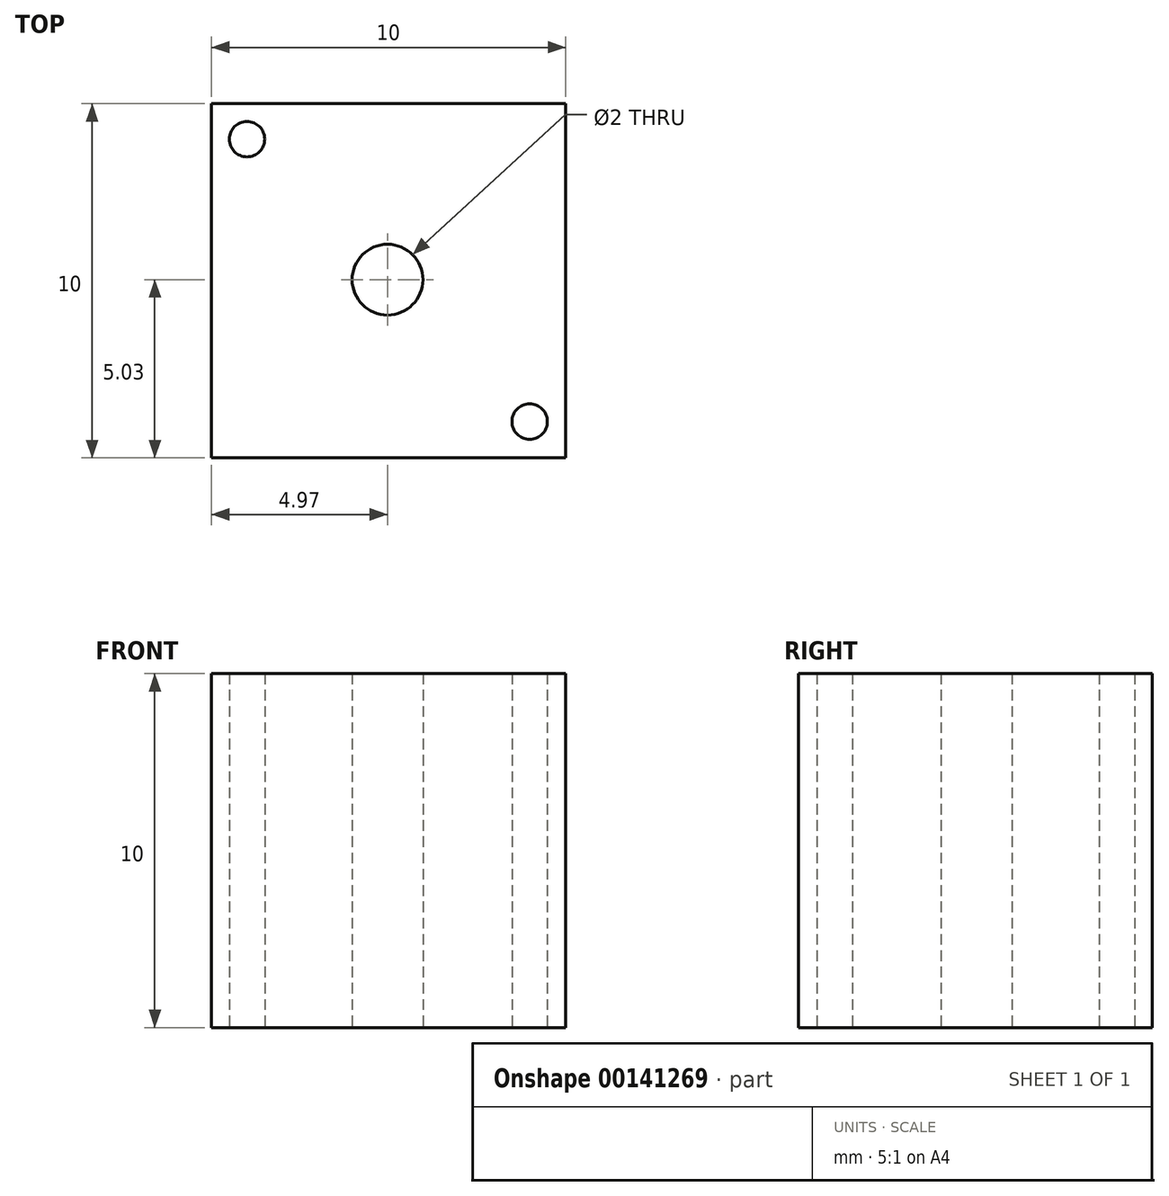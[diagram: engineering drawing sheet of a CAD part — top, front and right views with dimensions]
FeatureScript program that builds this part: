
annotation { "Feature Type Name" : "Feature", "Feature Type Description" : "" }
export const myFeature = defineFeature(function(context is Context, id is Id, definition is map)
    precondition{}
    {
        {
            var Q0;
            Q0=qCreatedBy(makeId("Top.planeOp"),FACE);
            var sketch = newSketch(context, id + "F0", { "sketchPlane" : qUnion([Q0])});
            skLineSegment(sketch, "E0.bottom", {"start": v(5.03, 4.97) * mm, "end": v(-4.97, 4.97) * mm});
            skLineSegment(sketch, "E0.top", {"start": v(5.03, -5.03) * mm, "end": v(-4.97, -5.03) * mm});
            skLineSegment(sketch, "E0.left", {"start": v(5.03, 4.97) * mm, "end": v(5.03, -5.03) * mm});
            skLineSegment(sketch, "E0.right", {"start": v(-4.97, 4.97) * mm, "end": v(-4.97, -5.03) * mm});
            skCircle(sketch, "E1", {"center": v(0, 0) * mm, "radius": 1 * mm});
            skLineSegment(sketch, "E2", {"start": v(-4.97, -0.03) * mm, "end": v(5.03, -0.03) * mm, "construction": true});
            skLineSegment(sketch, "E3", {"start": v(0, 4.97) * mm, "end": v(0.03, -5.03) * mm, "construction": true});
            skPoint(sketch, "E3.endSnap0", {"position": v(0.03, 4.97) * mm});
            skLineSegment(sketch, "E4", {"start": v(-4.97, -0.9) * mm, "end": v(-3.97, -0.9) * mm});
            skPoint(sketch, "E5", {"position": v(-3.97, -4.03) * mm});
            skCircle(sketch, "E6", {"center": v(-3.97, -4.03) * mm, "radius": 0.5 * mm});
            skCircle(sketch, "E7.MirrorC", {"center": v(4.02, -4) * mm, "radius": 0.5 * mm});
            skCircle(sketch, "E8.MirrorC", {"center": v(-3.97, 3.97) * mm, "radius": 0.5 * mm});
            skCircle(sketch, "E9.MirrorC", {"center": v(4.02, 3.95) * mm, "radius": 0.5 * mm});
            skSolve(sketch);
        }
        {
            var Q0;
            {var subQ1=sQuery(id+"F0.wireOp",EDGE,"E0.bottom");Q0=makeQuery(id+"F0.imprint","IMPRINT",FACE,{"disambiguationData":[TD([[makeQuery(id+"F0.imprint","IMPRINT",EDGE,{"derivedFrom":subQ1}),1.0]])]});}
            extrude(context, id + "F1", {"entities" : qUnion([Q0]), "depth" : 2 * mm});
        }
        {
            var Q0;
            Q0=makeQuery(id+"F0.imprint","IMPRINT",FACE,{"disambiguationData":[TD([[makeQuery(id+"F0.imprint","IMPRINT",EDGE,{"derivedFrom":sQuery(id+"F0.wireOp",EDGE,"E8.MirrorC")}),-1.0]])]});
            var Q1;
            Q1=makeQuery(id+"F0.imprint","IMPRINT",FACE,{"disambiguationData":[TD([[makeQuery(id+"F0.imprint","IMPRINT",EDGE,{"derivedFrom":sQuery(id+"F0.wireOp",EDGE,"E9.MirrorC")}),1.0]])]});
            var Q2;
            Q2=makeQuery(id+"F0.imprint","IMPRINT",FACE,{"disambiguationData":[TD([[makeQuery(id+"F0.imprint","IMPRINT",EDGE,{"derivedFrom":sQuery(id+"F0.wireOp",EDGE,"E7.MirrorC")}),-1.0]])]});
            var Q3;
            Q3=makeQuery(id+"F0.imprint","IMPRINT",FACE,{"disambiguationData":[TD([[makeQuery(id+"F0.imprint","IMPRINT",EDGE,{"derivedFrom":sQuery(id+"F0.wireOp",EDGE,"E6")}),1.0]])]});
            extrude(context, id + "F2", {"entities" : qUnion([Q0, Q1, Q2, Q3]), "operationType" : NewBodyOperationType.ADD, "depth" : 10 * mm});
        }
    });
